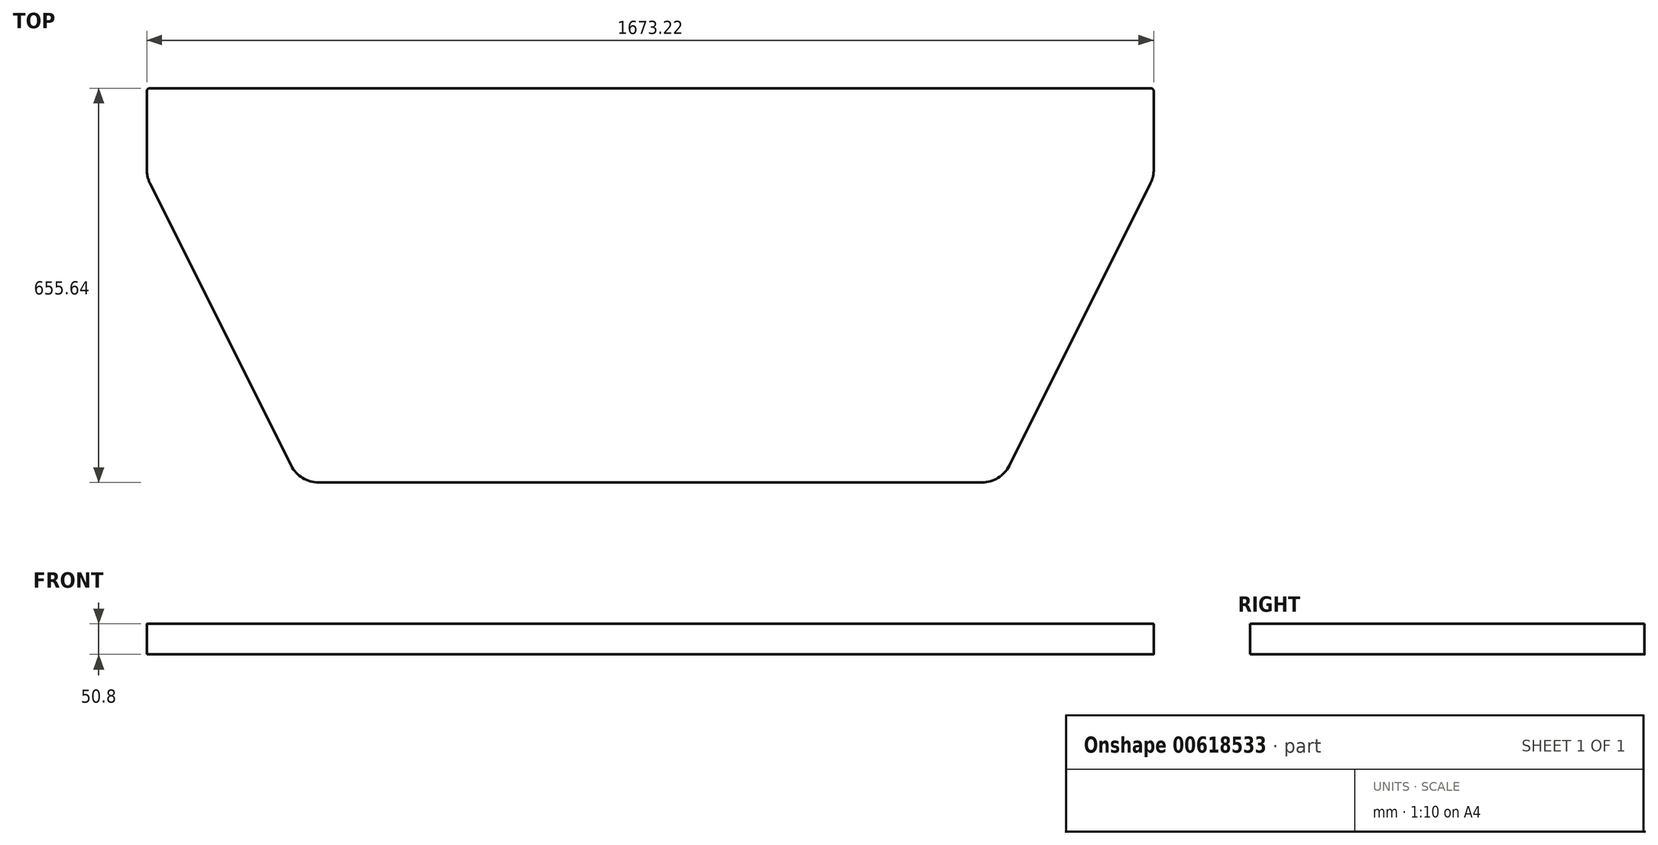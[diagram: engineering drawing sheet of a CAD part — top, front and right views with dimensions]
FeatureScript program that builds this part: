
annotation { "Feature Type Name" : "Feature", "Feature Type Description" : "" }
export const myFeature = defineFeature(function(context is Context, id is Id, definition is map)
    precondition{}
    {
        {
            var Q0;
            Q0=qCreatedBy(makeId("Top.planeOp"),FACE);
            var sketch = newSketch(context, id + "F0", { "sketchPlane" : qUnion([Q0])});
            skLineSegment(sketch, "E0", {"start": v(-836.61, 0) * mm, "end": v(836.61, 0) * mm});
            skLineSegment(sketch, "E1", {"start": v(836.61, 0) * mm, "end": v(836.61, -147.64) * mm});
            skLineSegment(sketch, "E2", {"start": v(-836.61, 0) * mm, "end": v(-836.61, -147.64) * mm});
            skLineSegment(sketch, "E3", {"start": v(-836.61, -147.64) * mm, "end": v(-582.61, -655.64) * mm});
            skLineSegment(sketch, "E4", {"start": v(-582.61, -655.64) * mm, "end": v(582.61, -655.64) * mm});
            skLineSegment(sketch, "E5", {"start": v(582.61, -655.64) * mm, "end": v(836.61, -147.64) * mm});
            skSolve(sketch);
        }
        {
            var Q0;
            Q0 = qSketchRegion(id + "F0", true);
            extrude(context, id + "F1", {"entities" : qUnion([Q0]), "oppositeDirection" : true, "depth" : 50.8 * mm, "offsetDistance" : 25.4 * mm});
        }
        {
            var Q0;
            Q0=makeQuery(id+"F1.opExtrude","SWEPT_EDGE",EDGE,{"disambiguationData":[OSD([sQuery(id+"F0.wireOp",EDGE,"E2"),sQuery(id+"F0.wireOp",EDGE,"E3")])]});
            var Q1;
            Q1=makeQuery(id+"F1.opExtrude","SWEPT_EDGE",EDGE,{"disambiguationData":[OSD([sQuery(id+"F0.wireOp",EDGE,"E3"),sQuery(id+"F0.wireOp",EDGE,"E4")])]});
            var Q2;
            Q2=makeQuery(id+"F1.opExtrude","SWEPT_EDGE",EDGE,{"disambiguationData":[OSD([sQuery(id+"F0.wireOp",EDGE,"E4"),sQuery(id+"F0.wireOp",EDGE,"E5")])]});
            var Q3;
            Q3=makeQuery(id+"F1.opExtrude","SWEPT_EDGE",EDGE,{"disambiguationData":[OSD([sQuery(id+"F0.wireOp",EDGE,"E1"),sQuery(id+"F0.wireOp",EDGE,"E5")])]});
            fillet(context, id + "F2", {"entities" : qUnion([Q0, Q1, Q2, Q3]), "radius" : 50.8 * mm, "tangentPropagation" : true, "allowEdgeOverflow" : false});
        }
        {
            var Q0;
            Q0=makeQuery(id+"F1.opExtrude","SWEPT_EDGE",EDGE,{"disambiguationData":[OSD([sQuery(id+"F0.wireOp",EDGE,"E0"),sQuery(id+"F0.wireOp",EDGE,"E1")])]});
            var Q1;
            Q1=makeQuery(id+"F1.opExtrude","SWEPT_EDGE",EDGE,{"disambiguationData":[OSD([sQuery(id+"F0.wireOp",EDGE,"E0"),sQuery(id+"F0.wireOp",EDGE,"E2")])]});
            fillet(context, id + "F3", {"entities" : qUnion([Q0, Q1]), "radius" : 5.08 * mm, "tangentPropagation" : true, "allowEdgeOverflow" : false});
        }
    });
